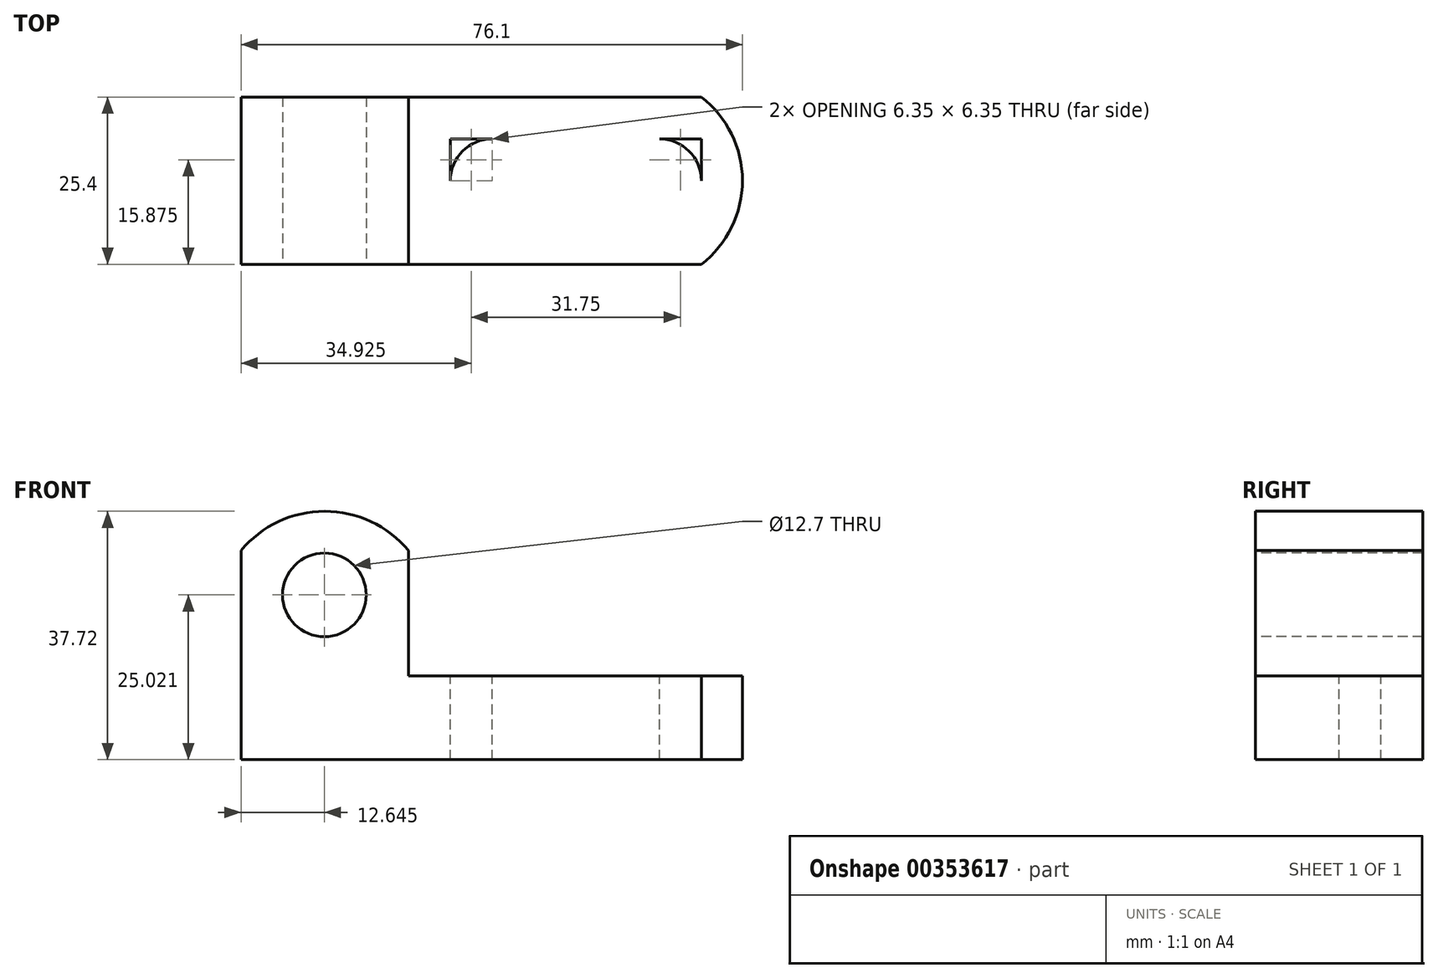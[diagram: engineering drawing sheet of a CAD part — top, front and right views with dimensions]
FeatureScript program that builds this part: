
annotation { "Feature Type Name" : "Feature", "Feature Type Description" : "" }
export const myFeature = defineFeature(function(context is Context, id is Id, definition is map)
    precondition{}
    {
        {
            var Q0;
            Q0=qCreatedBy(makeId("Front.planeOp"),FACE);
            var sketch = newSketch(context, id + "F0", { "sketchPlane" : qUnion([Q0])});
            skLineSegment(sketch, "E0", {"start": v(0, 0) * mm, "end": v(0, 38.1) * mm});
            skLineSegment(sketch, "E1", {"start": v(0, 38.1) * mm, "end": v(25.4, 38.1) * mm});
            skLineSegment(sketch, "E2", {"start": v(25.4, 38.1) * mm, "end": v(25.4, 12.7) * mm});
            skLineSegment(sketch, "E3", {"start": v(25.4, 12.7) * mm, "end": v(76.2, 12.7) * mm});
            skLineSegment(sketch, "E4", {"start": v(76.2, 12.7) * mm, "end": v(76.2, 0) * mm});
            skLineSegment(sketch, "E5", {"start": v(76.2, 0) * mm, "end": v(0, 0) * mm});
            skSolve(sketch);
        }
        {
            var Q0;
            Q0=makeQuery(id+"F0.imprint","IMPRINT",FACE,{"disambiguationData":[TD([[makeQuery(id+"F0.imprint","IMPRINT",EDGE,{"derivedFrom":sQuery(id+"F0.wireOp",EDGE,"E0")}),-1.0]])]});
            extrude(context, id + "F1", {"entities" : qUnion([Q0]), "depth" : 25.4 * mm});
        }
        {
            var Q0;
            Q0=makeQuery(id+"F1.opExtrude","CAP_FACE",FACE,{"disambiguationData":[OSD([sQuery(id+"F0.wireOp",EDGE,"E0"),sQuery(id+"F0.wireOp",EDGE,"E1"),sQuery(id+"F0.wireOp",EDGE,"E2"),sQuery(id+"F0.wireOp",EDGE,"E3"),sQuery(id+"F0.wireOp",EDGE,"E4"),sQuery(id+"F0.wireOp",EDGE,"E5")])],"isStart":false});
            var sketch = newSketch(context, id + "F2", { "sketchPlane" : qUnion([Q0])});
            skLineSegment(sketch, "E6", {"start": v(0, 31.75) * mm, "end": v(0, 38.1) * mm});
            skLineSegment(sketch, "E7", {"start": v(0, 38.1) * mm, "end": v(25.4, 38.1) * mm});
            skLineSegment(sketch, "E8", {"start": v(25.4, 38.1) * mm, "end": v(25.4, 31.75) * mm});
            skArc(sketch, "E9", {"start": v(25.4, 31.75) * mm, "mid": v(12.7, 37.72) * mm, "end": v(0, 31.75) * mm});
            skSolve(sketch);
        }
        {
            var Q0;
            Q0=makeQuery(id+"F2.imprint","IMPRINT",FACE,{"disambiguationData":[TD([[makeQuery(id+"F2.imprint","IMPRINT",EDGE,{"derivedFrom":sQuery(id+"F2.wireOp",EDGE,"E6")}),-1.0]])]});
            extrude(context, id + "F3", {"entities" : qUnion([Q0]), "operationType" : NewBodyOperationType.REMOVE, "oppositeDirection" : true, "depth" : 25.4 * mm});
        }
        {
            var Q0;
            Q0=makeQuery(id+"F1.opExtrude","SWEPT_FACE",FACE,{"disambiguationData":[OSD([sQuery(id+"F0.wireOp",EDGE,"E3")])]});
            var sketch = newSketch(context, id + "F4", { "sketchPlane" : qUnion([Q0])});
            skLineSegment(sketch, "E10.bottom", {"start": v(31.75, -6.35) * mm, "end": v(69.85, -6.35) * mm});
            skLineSegment(sketch, "E10.top", {"start": v(31.75, -19.05) * mm, "end": v(69.85, -19.05) * mm});
            skLineSegment(sketch, "E10.left", {"start": v(31.75, -6.35) * mm, "end": v(31.75, -19.05) * mm});
            skLineSegment(sketch, "E10.right", {"start": v(69.85, -6.35) * mm, "end": v(69.85, -19.05) * mm});
            skLineSegment(sketch, "E11", {"start": v(31.75, -6.35) * mm, "end": v(38.1, -6.35) * mm});
            skLineSegment(sketch, "E12", {"start": v(31.75, -19.05) * mm, "end": v(38.1, -19.05) * mm});
            skArc(sketch, "E13", {"start": v(38.1, -6.35) * mm, "mid": v(31.75, -12.7) * mm, "end": v(38.1, -19.05) * mm});
            skLineSegment(sketch, "E14", {"start": v(63.5, -6.35) * mm, "end": v(69.85, -6.35) * mm});
            skLineSegment(sketch, "E15", {"start": v(69.85, -19.05) * mm, "end": v(63.5, -19.05) * mm});
            skArc(sketch, "E16", {"start": v(63.5, -19.05) * mm, "mid": v(69.85, -12.7) * mm, "end": v(63.5, -6.35) * mm});
            skSolve(sketch);
        }
        {
            var Q0;
            {var subQ3=sQuery(id+"F4.wireOp",EDGE,"E10.bottom");Q0=makeQuery(id+"F4.imprint","IMPRINT",FACE,{"disambiguationData":[TD([[makeQuery(id+"F4.imprint","IMPRINT",EDGE,{"derivedFrom":subQ3}),-1.0]])]});}
            extrude(context, id + "F5", {"entities" : qUnion([Q0]), "operationType" : NewBodyOperationType.REMOVE, "oppositeDirection" : true, "depth" : 25.4 * mm});
        }
        {
            var Q0;
            Q0=makeQuery(id+"F1.opExtrude","CAP_FACE",FACE,{"disambiguationData":[OSD([sQuery(id+"F0.wireOp",EDGE,"E0"),sQuery(id+"F0.wireOp",EDGE,"E1"),sQuery(id+"F0.wireOp",EDGE,"E2"),sQuery(id+"F0.wireOp",EDGE,"E3"),sQuery(id+"F0.wireOp",EDGE,"E4"),sQuery(id+"F0.wireOp",EDGE,"E5")])],"isStart":false});
            var sketch = newSketch(context, id + "F6", { "sketchPlane" : qUnion([Q0])});
            skCircle(sketch, "E17", {"center": v(12.64, 25.02) * mm, "radius": 6.35 * mm});
            skSolve(sketch);
        }
        {
            var Q0;
            Q0=makeQuery(id+"F6.imprint","IMPRINT",FACE,{"disambiguationData":[TD([[makeQuery(id+"F6.imprint","IMPRINT",EDGE,{"derivedFrom":sQuery(id+"F6.wireOp",EDGE,"E17")}),1.0]])]});
            extrude(context, id + "F7", {"entities" : qUnion([Q0]), "operationType" : NewBodyOperationType.REMOVE, "oppositeDirection" : true, "depth" : 25.4 * mm});
        }
        {
            var Q0;
            Q0=makeQuery(id+"F1.opExtrude","SWEPT_FACE",FACE,{"disambiguationData":[OSD([sQuery(id+"F0.wireOp",EDGE,"E3")])]});
            var sketch = newSketch(context, id + "F8", { "sketchPlane" : qUnion([Q0])});
            skLineSegment(sketch, "E18", {"start": v(69.85, 0) * mm, "end": v(76.2, 0) * mm});
            skLineSegment(sketch, "E19", {"start": v(76.2, 0) * mm, "end": v(76.2, -25.4) * mm});
            skLineSegment(sketch, "E20", {"start": v(76.2, -25.4) * mm, "end": v(69.85, -25.4) * mm});
            skArc(sketch, "E21", {"start": v(69.85, -25.4) * mm, "mid": v(76.1, -12.7) * mm, "end": v(69.85, 0) * mm});
            skSolve(sketch);
        }
        {
            var Q0;
            Q0 = qSketchRegion(id + "F8", true);
            extrude(context, id + "F9", {"entities" : qUnion([Q0]), "operationType" : NewBodyOperationType.REMOVE, "oppositeDirection" : true, "depth" : 25.4 * mm});
        }
    });
